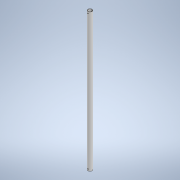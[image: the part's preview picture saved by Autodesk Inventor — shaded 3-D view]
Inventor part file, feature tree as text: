
AUTODESK INVENTOR PART (.ipt)
format: ipt  version: 2022 (Build 260153000, 153)  size: 169,984 bytes
history: native  units: mm
features: extrude x2, sketch x2
ambient origin geometry x8: Origin, YZ Plane, XZ Plane, XY Plane, X Axis, Y Axis, Z Axis, Center Point
bodies: Body1 (feature_tree)
feature tree (4):
  extrude  "Extrusion5"  Depth=15.0mm
  extrude  "Extrusion6"  Depth=6.0mm TaperAngle=0.0deg
  sketch  "Sketch2"  dims[d31=34.456mm d91=15.0mm]
  sketch  "Sketch3"  dims[d92=13.0mm d93=500.0mm d94=0.0mm d95=6.0mm d96=3.0mm d97=20.0mm d98=10.0mm d99=0.0mm d100=0.0mm d101=6.0mm d102=3.0mm]
